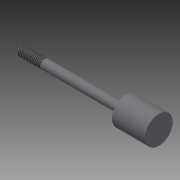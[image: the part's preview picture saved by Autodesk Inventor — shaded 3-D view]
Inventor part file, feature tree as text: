
AUTODESK INVENTOR PART (.ipt)
format: ipt  version: 2014 (Build 180170000, 170)  size: 130,560 bytes
history: native  units: in
note: dims shown in document units (in); Inventor stores cm internally (conversion verified against a paired STEP export)
features: other x49, revolve x3, sketch x3, thread x1
ambient origin geometry x8: Origin, YZ Plane, XZ Plane, XY Plane, X Axis, Y Axis, Z Axis, Center Point
bodies: Solid1 (feature_tree)
feature tree (56):
  revolve  "Revolution1"  [1 undecoded]
  thread  "Thread1"  [1 undecoded]
  revolve  "Revolution2"  [1 undecoded]
  revolve  "Revolution3"  [1 undecoded]
  other  "h1_XY"
  other  "h1_YZ"
  other  "h1_ZX"
  other  "h1_X"
  other  "h1_Y"
  other  "h1_Z"
  other  "h1_Center"
  other  "h2_XY"
  other  "h2_YZ"
  other  "h2_ZX"
  other  "h2_X"
  other  "h2_Y"
  other  "h2_Z"
  other  "h2_Center"
  other  "k1_XY"
  other  "k1_YZ"
  other  "k1_ZX"
  other  "k1_X"
  other  "k1_Y"
  other  "k1_Z"
  other  "k1_Center"
  other  "k2_XY"
  other  "k2_YZ"
  other  "k2_ZX"
  other  "k2_X"
  other  "k2_Y"
  other  "k2_Z"
  other  "k2_Center"
  other  "start_XY"
  other  "start_YZ"
  other  "start_ZX"
  other  "start_X"
  other  "start_Y"
  other  "start_Z"
  other  "start_Center"
  other  "to_prc_XY"
  other  "to_prc_YZ"
  other  "to_prc_ZX"
  other  "to_prc_X"
  other  "to_prc_Y"
  other  "to_prc_Z"
  other  "to_prc_Center"
  other  "to_rod_guide_XY"
  other  "to_rod_guide_YZ"
  other  "to_rod_guide_ZX"
  other  "to_rod_guide_X"
  other  "to_rod_guide_Y"
  other  "to_rod_guide_Z"
  other  "to_rod_guide_Center"
  sketch  "Sketch_3"  dims[d0=360.0deg d1=0.49in d2=2.302in d3=360.0deg]
  sketch  "Sketch_17"
  sketch  "Sketch_12"  dims[d4=360.0deg]
note: 4 required parameter values undecoded (feature->parameter linkage not recoverable at this tier; creation-order binding heuristic only, values carry confidence <= 0.55)